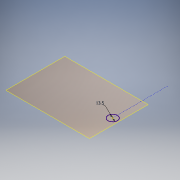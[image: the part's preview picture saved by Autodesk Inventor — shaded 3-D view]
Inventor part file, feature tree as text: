
AUTODESK INVENTOR PART (.ipt)
format: ipt  version: 2017 (Build 210142000, 142)  size: 87,040 bytes
history: native  units: mm
features: plane x1, sketch x1
ambient origin geometry x8: Origin, YZ Plane, XZ Plane, XY Plane, X Axis, Y Axis, Z Axis, Center Point
feature tree (2):
  plane  "Work Plane1"
  sketch  "Sketch1"  dims[d0=13.5mm d1=65.0mm]
